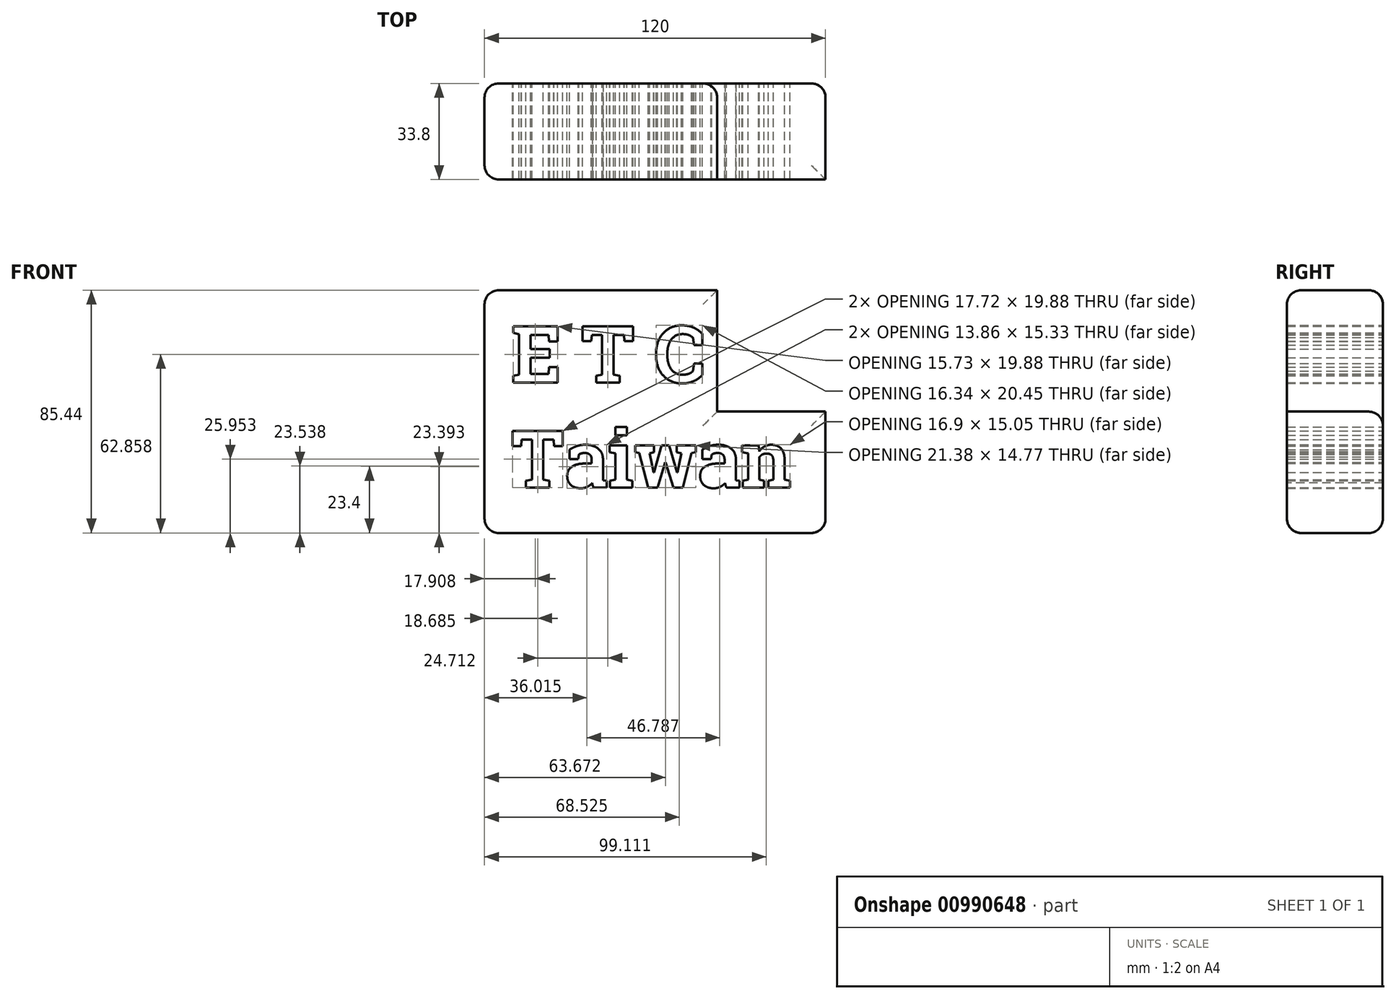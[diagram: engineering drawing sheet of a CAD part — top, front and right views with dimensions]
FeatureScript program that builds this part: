
annotation { "Feature Type Name" : "Feature", "Feature Type Description" : "" }
export const myFeature = defineFeature(function(context is Context, id is Id, definition is map)
    precondition{}
    {
        {
            var Q0;
            Q0=qCreatedBy(makeId("Front.planeOp"),FACE);
            var sketch = newSketch(context, id + "F0", { "sketchPlane" : qUnion([Q0])});
            skLineSegment(sketch, "E0.bottom", {"start": v(60, -42.72) * mm, "end": v(-60, -42.72) * mm});
            skLineSegment(sketch, "E0.top", {"start": v(60, 42.72) * mm, "end": v(-60, 42.72) * mm});
            skLineSegment(sketch, "E0.left", {"start": v(60, -42.72) * mm, "end": v(60, 42.72) * mm});
            skLineSegment(sketch, "E0.right", {"start": v(-60, -42.72) * mm, "end": v(-60, 42.72) * mm});
            skPoint(sketch, "E0.middle", {"position": v(0, 0) * mm});
            skText(sketch, "E1", { "text": "E T C \nTaiwan", "fontName": "RobotoSlab-Bold.ttf"});
            const initialGuessF0  = {"E1": [-0.05072, 0.0102, 1, 0, 0.02013]};
            skSetInitialGuess(sketch, initialGuessF0);
            skSolve(sketch);
        }
        {
            var Q0;
            Q0=makeQuery(id+"F0.imprint","IMPRINT",FACE,{"disambiguationData":[TD([[makeQuery(id+"F0.imprint","IMPRINT",EDGE,{"derivedFrom":sQuery(id+"F0.wireOp",EDGE,"E0.bottom")}),-1.0]])]});
            extrude(context, id + "F1", {"entities" : qUnion([Q0]), "depth" : 3.2 * mm, "offsetDistance" : 25 * mm});
        }
        {
            var Q0;
            Q0 = qSketchRegion(id + "F0", true);
            extrude(context, id + "F2", {"entities" : qUnion([Q0]), "operationType" : NewBodyOperationType.ADD, "oppositeDirection" : true, "depth" : 30.6 * mm, "offsetDistance" : 25 * mm});
        }
        {
            var Q0;
            Q0=makeQuery(id+"F1.opExtrude","CAP_FACE",FACE,{"disambiguationData":[OSD([sQuery(id+"F0.wireOp",EDGE,"E0.bottom"),sQuery(id+"F0.wireOp",EDGE,"E0.top"),sQuery(id+"F0.wireOp",EDGE,"E0.left"),sQuery(id+"F0.wireOp",EDGE,"E0.right"),sQuery(id+"F0.wireOp",EDGE,"E1.sketch_text.stroke-0"),sQuery(id+"F0.wireOp",EDGE,"E1.sketch_text.stroke-1"),sQuery(id+"F0.wireOp",EDGE,"E1.sketch_text.stroke-2"),sQuery(id+"F0.wireOp",EDGE,"E1.sketch_text.stroke-3"),sQuery(id+"F0.wireOp",EDGE,"E1.sketch_text.stroke-4"),sQuery(id+"F0.wireOp",EDGE,"E1.sketch_text.stroke-5"),sQuery(id+"F0.wireOp",EDGE,"E1.sketch_text.stroke-6"),sQuery(id+"F0.wireOp",EDGE,"E1.sketch_text.stroke-7"),sQuery(id+"F0.wireOp",EDGE,"E1.sketch_text.stroke-8"),sQuery(id+"F0.wireOp",EDGE,"E1.sketch_text.stroke-9"),sQuery(id+"F0.wireOp",EDGE,"E1.sketch_text.stroke-10"),sQuery(id+"F0.wireOp",EDGE,"E1.sketch_text.stroke-11"),sQuery(id+"F0.wireOp",EDGE,"E1.sketch_text.stroke-12"),sQuery(id+"F0.wireOp",EDGE,"E1.sketch_text.stroke-13"),sQuery(id+"F0.wireOp",EDGE,"E1.sketch_text.stroke-14"),sQuery(id+"F0.wireOp",EDGE,"E1.sketch_text.stroke-15"),sQuery(id+"F0.wireOp",EDGE,"E1.sketch_text.stroke-16"),sQuery(id+"F0.wireOp",EDGE,"E1.sketch_text.stroke-17"),sQuery(id+"F0.wireOp",EDGE,"E1.sketch_text.stroke-18"),sQuery(id+"F0.wireOp",EDGE,"E1.sketch_text.stroke-19"),sQuery(id+"F0.wireOp",EDGE,"E1.sketch_text.stroke-20"),sQuery(id+"F0.wireOp",EDGE,"E1.sketch_text.stroke-21"),sQuery(id+"F0.wireOp",EDGE,"E1.sketch_text.stroke-22"),sQuery(id+"F0.wireOp",EDGE,"E1.sketch_text.stroke-23"),sQuery(id+"F0.wireOp",EDGE,"E1.sketch_text.stroke-24"),sQuery(id+"F0.wireOp",EDGE,"E1.sketch_text.stroke-25"),sQuery(id+"F0.wireOp",EDGE,"E1.sketch_text.stroke-26"),sQuery(id+"F0.wireOp",EDGE,"E1.sketch_text.stroke-27"),sQuery(id+"F0.wireOp",EDGE,"E1.sketch_text.stroke-28"),sQuery(id+"F0.wireOp",EDGE,"E1.sketch_text.stroke-29"),sQuery(id+"F0.wireOp",EDGE,"E1.sketch_text.stroke-30"),sQuery(id+"F0.wireOp",EDGE,"E1.sketch_text.stroke-31"),sQuery(id+"F0.wireOp",EDGE,"E1.sketch_text.stroke-32"),sQuery(id+"F0.wireOp",EDGE,"E1.sketch_text.stroke-33"),sQuery(id+"F0.wireOp",EDGE,"E1.sketch_text.stroke-34"),sQuery(id+"F0.wireOp",EDGE,"E1.sketch_text.stroke-35"),sQuery(id+"F0.wireOp",EDGE,"E1.sketch_text.stroke-36"),sQuery(id+"F0.wireOp",EDGE,"E1.sketch_text.stroke-37"),sQuery(id+"F0.wireOp",EDGE,"E1.sketch_text.stroke-38"),sQuery(id+"F0.wireOp",EDGE,"E1.sketch_text.stroke-39"),sQuery(id+"F0.wireOp",EDGE,"E1.sketch_text.stroke-40"),sQuery(id+"F0.wireOp",EDGE,"E1.sketch_text.stroke-41"),sQuery(id+"F0.wireOp",EDGE,"E1.sketch_text.stroke-42"),sQuery(id+"F0.wireOp",EDGE,"E1.sketch_text.stroke-43"),sQuery(id+"F0.wireOp",EDGE,"E1.sketch_text.stroke-44"),sQuery(id+"F0.wireOp",EDGE,"E1.sketch_text.stroke-45"),sQuery(id+"F0.wireOp",EDGE,"E1.sketch_text.stroke-46"),sQuery(id+"F0.wireOp",EDGE,"E1.sketch_text.stroke-47"),sQuery(id+"F0.wireOp",EDGE,"E1.sketch_text.stroke-48"),sQuery(id+"F0.wireOp",EDGE,"E1.sketch_text.stroke-49"),sQuery(id+"F0.wireOp",EDGE,"E1.sketch_text.stroke-50"),sQuery(id+"F0.wireOp",EDGE,"E1.sketch_text.stroke-51"),sQuery(id+"F0.wireOp",EDGE,"E1.sketch_text.stroke-52"),sQuery(id+"F0.wireOp",EDGE,"E1.sketch_text.stroke-53"),sQuery(id+"F0.wireOp",EDGE,"E1.sketch_text.stroke-54"),sQuery(id+"F0.wireOp",EDGE,"E1.sketch_text.stroke-55"),sQuery(id+"F0.wireOp",EDGE,"E1.sketch_text.stroke-56"),sQuery(id+"F0.wireOp",EDGE,"E1.sketch_text.stroke-57"),sQuery(id+"F0.wireOp",EDGE,"E1.sketch_text.stroke-58"),sQuery(id+"F0.wireOp",EDGE,"E1.sketch_text.stroke-59"),sQuery(id+"F0.wireOp",EDGE,"E1.sketch_text.stroke-60"),sQuery(id+"F0.wireOp",EDGE,"E1.sketch_text.stroke-61"),sQuery(id+"F0.wireOp",EDGE,"E1.sketch_text.stroke-62"),sQuery(id+"F0.wireOp",EDGE,"E1.sketch_text.stroke-63"),sQuery(id+"F0.wireOp",EDGE,"E1.sketch_text.stroke-64"),sQuery(id+"F0.wireOp",EDGE,"E1.sketch_text.stroke-65"),sQuery(id+"F0.wireOp",EDGE,"E1.sketch_text.stroke-66"),sQuery(id+"F0.wireOp",EDGE,"E1.sketch_text.stroke-67"),sQuery(id+"F0.wireOp",EDGE,"E1.sketch_text.stroke-68"),sQuery(id+"F0.wireOp",EDGE,"E1.sketch_text.stroke-69"),sQuery(id+"F0.wireOp",EDGE,"E1.sketch_text.stroke-70"),sQuery(id+"F0.wireOp",EDGE,"E1.sketch_text.stroke-71"),sQuery(id+"F0.wireOp",EDGE,"E1.sketch_text.stroke-72"),sQuery(id+"F0.wireOp",EDGE,"E1.sketch_text.stroke-73"),sQuery(id+"F0.wireOp",EDGE,"E1.sketch_text.stroke-74"),sQuery(id+"F0.wireOp",EDGE,"E1.sketch_text.stroke-75"),sQuery(id+"F0.wireOp",EDGE,"E1.sketch_text.stroke-76"),sQuery(id+"F0.wireOp",EDGE,"E1.sketch_text.stroke-77"),sQuery(id+"F0.wireOp",EDGE,"E1.sketch_text.stroke-78"),sQuery(id+"F0.wireOp",EDGE,"E1.sketch_text.stroke-79"),sQuery(id+"F0.wireOp",EDGE,"E1.sketch_text.stroke-80"),sQuery(id+"F0.wireOp",EDGE,"E1.sketch_text.stroke-81"),sQuery(id+"F0.wireOp",EDGE,"E1.sketch_text.stroke-82"),sQuery(id+"F0.wireOp",EDGE,"E1.sketch_text.stroke-83"),sQuery(id+"F0.wireOp",EDGE,"E1.sketch_text.stroke-84"),sQuery(id+"F0.wireOp",EDGE,"E1.sketch_text.stroke-85"),sQuery(id+"F0.wireOp",EDGE,"E1.sketch_text.stroke-86"),sQuery(id+"F0.wireOp",EDGE,"E1.sketch_text.stroke-87"),sQuery(id+"F0.wireOp",EDGE,"E1.sketch_text.stroke-88"),sQuery(id+"F0.wireOp",EDGE,"E1.sketch_text.stroke-89"),sQuery(id+"F0.wireOp",EDGE,"E1.sketch_text.stroke-90"),sQuery(id+"F0.wireOp",EDGE,"E1.sketch_text.stroke-91"),sQuery(id+"F0.wireOp",EDGE,"E1.sketch_text.stroke-92"),sQuery(id+"F0.wireOp",EDGE,"E1.sketch_text.stroke-93"),sQuery(id+"F0.wireOp",EDGE,"E1.sketch_text.stroke-94"),sQuery(id+"F0.wireOp",EDGE,"E1.sketch_text.stroke-95"),sQuery(id+"F0.wireOp",EDGE,"E1.sketch_text.stroke-96"),sQuery(id+"F0.wireOp",EDGE,"E1.sketch_text.stroke-97"),sQuery(id+"F0.wireOp",EDGE,"E1.sketch_text.stroke-98"),sQuery(id+"F0.wireOp",EDGE,"E1.sketch_text.stroke-99"),sQuery(id+"F0.wireOp",EDGE,"E1.sketch_text.stroke-100"),sQuery(id+"F0.wireOp",EDGE,"E1.sketch_text.stroke-101"),sQuery(id+"F0.wireOp",EDGE,"E1.sketch_text.stroke-102"),sQuery(id+"F0.wireOp",EDGE,"E1.sketch_text.stroke-103"),sQuery(id+"F0.wireOp",EDGE,"E1.sketch_text.stroke-112"),sQuery(id+"F0.wireOp",EDGE,"E1.sketch_text.stroke-113"),sQuery(id+"F0.wireOp",EDGE,"E1.sketch_text.stroke-114"),sQuery(id+"F0.wireOp",EDGE,"E1.sketch_text.stroke-115"),sQuery(id+"F0.wireOp",EDGE,"E1.sketch_text.stroke-116"),sQuery(id+"F0.wireOp",EDGE,"E1.sketch_text.stroke-117"),sQuery(id+"F0.wireOp",EDGE,"E1.sketch_text.stroke-118"),sQuery(id+"F0.wireOp",EDGE,"E1.sketch_text.stroke-119"),sQuery(id+"F0.wireOp",EDGE,"E1.sketch_text.stroke-120"),sQuery(id+"F0.wireOp",EDGE,"E1.sketch_text.stroke-121"),sQuery(id+"F0.wireOp",EDGE,"E1.sketch_text.stroke-122"),sQuery(id+"F0.wireOp",EDGE,"E1.sketch_text.stroke-123"),sQuery(id+"F0.wireOp",EDGE,"E1.sketch_text.stroke-124"),sQuery(id+"F0.wireOp",EDGE,"E1.sketch_text.stroke-125"),sQuery(id+"F0.wireOp",EDGE,"E1.sketch_text.stroke-126"),sQuery(id+"F0.wireOp",EDGE,"E1.sketch_text.stroke-127"),sQuery(id+"F0.wireOp",EDGE,"E1.sketch_text.stroke-128"),sQuery(id+"F0.wireOp",EDGE,"E1.sketch_text.stroke-129"),sQuery(id+"F0.wireOp",EDGE,"E1.sketch_text.stroke-130"),sQuery(id+"F0.wireOp",EDGE,"E1.sketch_text.stroke-131"),sQuery(id+"F0.wireOp",EDGE,"E1.sketch_text.stroke-132"),sQuery(id+"F0.wireOp",EDGE,"E1.sketch_text.stroke-133"),sQuery(id+"F0.wireOp",EDGE,"E1.sketch_text.stroke-134"),sQuery(id+"F0.wireOp",EDGE,"E1.sketch_text.stroke-135"),sQuery(id+"F0.wireOp",EDGE,"E1.sketch_text.stroke-136"),sQuery(id+"F0.wireOp",EDGE,"E1.sketch_text.stroke-137"),sQuery(id+"F0.wireOp",EDGE,"E1.sketch_text.stroke-138"),sQuery(id+"F0.wireOp",EDGE,"E1.sketch_text.stroke-139"),sQuery(id+"F0.wireOp",EDGE,"E1.sketch_text.stroke-140"),sQuery(id+"F0.wireOp",EDGE,"E1.sketch_text.stroke-141"),sQuery(id+"F0.wireOp",EDGE,"E1.sketch_text.stroke-142"),sQuery(id+"F0.wireOp",EDGE,"E1.sketch_text.stroke-143"),sQuery(id+"F0.wireOp",EDGE,"E1.sketch_text.stroke-144"),sQuery(id+"F0.wireOp",EDGE,"E1.sketch_text.stroke-145"),sQuery(id+"F0.wireOp",EDGE,"E1.sketch_text.stroke-146"),sQuery(id+"F0.wireOp",EDGE,"E1.sketch_text.stroke-147"),sQuery(id+"F0.wireOp",EDGE,"E1.sketch_text.stroke-148"),sQuery(id+"F0.wireOp",EDGE,"E1.sketch_text.stroke-149"),sQuery(id+"F0.wireOp",EDGE,"E1.sketch_text.stroke-150"),sQuery(id+"F0.wireOp",EDGE,"E1.sketch_text.stroke-151"),sQuery(id+"F0.wireOp",EDGE,"E1.sketch_text.stroke-152"),sQuery(id+"F0.wireOp",EDGE,"E1.sketch_text.stroke-153"),sQuery(id+"F0.wireOp",EDGE,"E1.sketch_text.stroke-154"),sQuery(id+"F0.wireOp",EDGE,"E1.sketch_text.stroke-155"),sQuery(id+"F0.wireOp",EDGE,"E1.sketch_text.stroke-156"),sQuery(id+"F0.wireOp",EDGE,"E1.sketch_text.stroke-157"),sQuery(id+"F0.wireOp",EDGE,"E1.sketch_text.stroke-158"),sQuery(id+"F0.wireOp",EDGE,"E1.sketch_text.stroke-159"),sQuery(id+"F0.wireOp",EDGE,"E1.sketch_text.stroke-160"),sQuery(id+"F0.wireOp",EDGE,"E1.sketch_text.stroke-161"),sQuery(id+"F0.wireOp",EDGE,"E1.sketch_text.stroke-162"),sQuery(id+"F0.wireOp",EDGE,"E1.sketch_text.stroke-163"),sQuery(id+"F0.wireOp",EDGE,"E1.sketch_text.stroke-164"),sQuery(id+"F0.wireOp",EDGE,"E1.sketch_text.stroke-165"),sQuery(id+"F0.wireOp",EDGE,"E1.sketch_text.stroke-166"),sQuery(id+"F0.wireOp",EDGE,"E1.sketch_text.stroke-167"),sQuery(id+"F0.wireOp",EDGE,"E1.sketch_text.stroke-168"),sQuery(id+"F0.wireOp",EDGE,"E1.sketch_text.stroke-169"),sQuery(id+"F0.wireOp",EDGE,"E1.sketch_text.stroke-170"),sQuery(id+"F0.wireOp",EDGE,"E1.sketch_text.stroke-171"),sQuery(id+"F0.wireOp",EDGE,"E1.sketch_text.stroke-172"),sQuery(id+"F0.wireOp",EDGE,"E1.sketch_text.stroke-173"),sQuery(id+"F0.wireOp",EDGE,"E1.sketch_text.stroke-174"),sQuery(id+"F0.wireOp",EDGE,"E1.sketch_text.stroke-175"),sQuery(id+"F0.wireOp",EDGE,"E1.sketch_text.stroke-176"),sQuery(id+"F0.wireOp",EDGE,"E1.sketch_text.stroke-185"),sQuery(id+"F0.wireOp",EDGE,"E1.sketch_text.stroke-186"),sQuery(id+"F0.wireOp",EDGE,"E1.sketch_text.stroke-187"),sQuery(id+"F0.wireOp",EDGE,"E1.sketch_text.stroke-188"),sQuery(id+"F0.wireOp",EDGE,"E1.sketch_text.stroke-189"),sQuery(id+"F0.wireOp",EDGE,"E1.sketch_text.stroke-190"),sQuery(id+"F0.wireOp",EDGE,"E1.sketch_text.stroke-191"),sQuery(id+"F0.wireOp",EDGE,"E1.sketch_text.stroke-192"),sQuery(id+"F0.wireOp",EDGE,"E1.sketch_text.stroke-193"),sQuery(id+"F0.wireOp",EDGE,"E1.sketch_text.stroke-194"),sQuery(id+"F0.wireOp",EDGE,"E1.sketch_text.stroke-195"),sQuery(id+"F0.wireOp",EDGE,"E1.sketch_text.stroke-196"),sQuery(id+"F0.wireOp",EDGE,"E1.sketch_text.stroke-197"),sQuery(id+"F0.wireOp",EDGE,"E1.sketch_text.stroke-198"),sQuery(id+"F0.wireOp",EDGE,"E1.sketch_text.stroke-199"),sQuery(id+"F0.wireOp",EDGE,"E1.sketch_text.stroke-200"),sQuery(id+"F0.wireOp",EDGE,"E1.sketch_text.stroke-201"),sQuery(id+"F0.wireOp",EDGE,"E1.sketch_text.stroke-202"),sQuery(id+"F0.wireOp",EDGE,"E1.sketch_text.stroke-203"),sQuery(id+"F0.wireOp",EDGE,"E1.sketch_text.stroke-204"),sQuery(id+"F0.wireOp",EDGE,"E1.sketch_text.stroke-205"),sQuery(id+"F0.wireOp",EDGE,"E1.sketch_text.stroke-206"),sQuery(id+"F0.wireOp",EDGE,"E1.sketch_text.stroke-207"),sQuery(id+"F0.wireOp",EDGE,"E1.sketch_text.stroke-208"),sQuery(id+"F0.wireOp",EDGE,"E1.sketch_text.stroke-209"),sQuery(id+"F0.wireOp",EDGE,"E1.sketch_text.stroke-210")])],"isStart":false});
            var sketch = newSketch(context, id + "F3", { "sketchPlane" : qUnion([Q0])});
            skLineSegment(sketch, "E2.bottom", {"start": v(60, 42.72) * mm, "end": v(21.87, 42.72) * mm});
            skLineSegment(sketch, "E2.top", {"start": v(60, 0) * mm, "end": v(21.87, 0) * mm});
            skLineSegment(sketch, "E2.left", {"start": v(60, 42.72) * mm, "end": v(60, 0) * mm});
            skLineSegment(sketch, "E2.right", {"start": v(21.87, 42.72) * mm, "end": v(21.87, 0) * mm});
            skSolve(sketch);
        }
        {
            var Q0;
            Q0=makeQuery(id+"F3.imprint","IMPRINT",FACE,{"disambiguationData":[TD([[makeQuery(id+"F3.imprint","IMPRINT",EDGE,{"derivedFrom":sQuery(id+"F3.wireOp",EDGE,"E2.bottom")}),1.0]])]});
            extrude(context, id + "F4", {"entities" : qUnion([Q0]), "operationType" : NewBodyOperationType.REMOVE, "oppositeDirection" : true, "depth" : 35.3 * mm, "offsetDistance" : 25 * mm});
        }
        {
            var Q0;
            Q0=makeQuery(id+"F4.boolean.opBoolean","COPY",EDGE,{"derivedFrom":makeQuery(id+"F4.opExtrude","SWEPT_EDGE",EDGE,{"disambiguationData":[OSD([sQuery(id+"F0.wireOp",EDGE,"E0.top"),sQuery(id+"F3.wireOp",EDGE,"E2.bottom"),sQuery(id+"F3.wireOp",EDGE,"E2.right")])]})});
            var Q1;
            Q1=makeQuery(id+"F4.boolean.opBoolean","COPY",EDGE,{"derivedFrom":makeQuery(id+"F4.opExtrude","SWEPT_EDGE",EDGE,{"disambiguationData":[OSD([sQuery(id+"F0.wireOp",EDGE,"E0.left"),sQuery(id+"F3.wireOp",EDGE,"E2.top"),sQuery(id+"F3.wireOp",EDGE,"E2.left")])]})});
            var Q2;
            {var subQ0=sQuery(id+"F0.wireOp",EDGE,"E0.left");var subQ1=sQuery(id+"F0.wireOp",EDGE,"E0.bottom");Q2=makeQuery(id+"F2.boolean.opBoolean","MERGE",EDGE,{"derivedFrom":[makeQuery(id+"F1.opExtrude","SWEPT_EDGE",EDGE,{"disambiguationData":[OSD([subQ1,subQ0])]}),makeQuery(id+"F2.opExtrude","SWEPT_EDGE",EDGE,{"disambiguationData":[OSD([subQ1,subQ0])]})]});}
            var Q3;
            {var subQ0=sQuery(id+"F0.wireOp",EDGE,"E0.bottom");Q3=makeQuery(id+"F2.boolean.opBoolean","MERGE",FACE,{"derivedFrom":[makeQuery(id+"F1.opExtrude","SWEPT_FACE",FACE,{"disambiguationData":[OSD([subQ0])]}),makeQuery(id+"F2.opExtrude","SWEPT_FACE",FACE,{"disambiguationData":[OSD([subQ0])]})]});}
            var Q4;
            {var subQ0=sQuery(id+"F0.wireOp",EDGE,"E0.right");var subQ1=sQuery(id+"F0.wireOp",EDGE,"E0.bottom");Q4=makeQuery(id+"F2.boolean.opBoolean","MERGE",EDGE,{"derivedFrom":[makeQuery(id+"F1.opExtrude","SWEPT_EDGE",EDGE,{"disambiguationData":[OSD([subQ1,subQ0])]}),makeQuery(id+"F2.opExtrude","SWEPT_EDGE",EDGE,{"disambiguationData":[OSD([subQ1,subQ0])]})]});}
            var Q5;
            Q5=makeQuery(id+"F1.opExtrude","CAP_EDGE",EDGE,{"disambiguationData":[OSD([sQuery(id+"F0.wireOp",EDGE,"E0.right")])],"isStart":false});
            var Q6;
            Q6=makeQuery(id+"F2.opExtrude","CAP_EDGE",EDGE,{"disambiguationData":[OSD([sQuery(id+"F0.wireOp",EDGE,"E0.right")])],"isStart":false});
            var Q7;
            {var subQ0=sQuery(id+"F0.wireOp",EDGE,"E0.right");var subQ1=sQuery(id+"F0.wireOp",EDGE,"E0.top");Q7=makeQuery(id+"F2.boolean.opBoolean","MERGE",EDGE,{"derivedFrom":[makeQuery(id+"F1.opExtrude","SWEPT_EDGE",EDGE,{"disambiguationData":[OSD([subQ1,subQ0])]}),makeQuery(id+"F2.opExtrude","SWEPT_EDGE",EDGE,{"disambiguationData":[OSD([subQ1,subQ0])]})]});}
            var Q8;
            Q8=makeQuery(id+"F1.opExtrude","CAP_EDGE",EDGE,{"disambiguationData":[OSD([sQuery(id+"F0.wireOp",EDGE,"E0.top")])],"isStart":false});
            var Q9;
            Q9=makeQuery(id+"F2.opExtrude","CAP_EDGE",EDGE,{"disambiguationData":[OSD([sQuery(id+"F0.wireOp",EDGE,"E0.top")])],"isStart":false});
            var Q10;
            Q10=makeQuery(id+"F4.boolean.opBoolean","COPY",EDGE,{"derivedFrom":makeQuery(id+"F4.opExtrude","CAP_EDGE",EDGE,{"disambiguationData":[OSD([sQuery(id+"F3.wireOp",EDGE,"E2.top")])],"isStart":true})});
            var Q11;
            Q11=makeQuery(id+"F4.boolean.opBoolean","COPY",EDGE,{"derivedFrom":makeQuery(id+"F4.opExtrude","CAP_EDGE",EDGE,{"disambiguationData":[OSD([sQuery(id+"F3.wireOp",EDGE,"E2.right")])],"isStart":true})});
            var Q12;
            Q12=makeQuery(id+"F2.opExtrude","CAP_EDGE",EDGE,{"disambiguationData":[OSD([sQuery(id+"F0.wireOp",EDGE,"E0.left")])],"isStart":false});
            var Q13;
            Q13=makeQuery(id+"F4.boolean.opBoolean","INTERSECT",EDGE,{"derivedFrom":[makeQuery(id+"F2.opExtrude","CAP_FACE",FACE,{"disambiguationData":[OSD([sQuery(id+"F0.wireOp",EDGE,"E0.bottom"),sQuery(id+"F0.wireOp",EDGE,"E0.top"),sQuery(id+"F0.wireOp",EDGE,"E0.left"),sQuery(id+"F0.wireOp",EDGE,"E0.right"),sQuery(id+"F0.wireOp",EDGE,"E1.sketch_text.stroke-0"),sQuery(id+"F0.wireOp",EDGE,"E1.sketch_text.stroke-1"),sQuery(id+"F0.wireOp",EDGE,"E1.sketch_text.stroke-2"),sQuery(id+"F0.wireOp",EDGE,"E1.sketch_text.stroke-3"),sQuery(id+"F0.wireOp",EDGE,"E1.sketch_text.stroke-4"),sQuery(id+"F0.wireOp",EDGE,"E1.sketch_text.stroke-5"),sQuery(id+"F0.wireOp",EDGE,"E1.sketch_text.stroke-6"),sQuery(id+"F0.wireOp",EDGE,"E1.sketch_text.stroke-7"),sQuery(id+"F0.wireOp",EDGE,"E1.sketch_text.stroke-8"),sQuery(id+"F0.wireOp",EDGE,"E1.sketch_text.stroke-9"),sQuery(id+"F0.wireOp",EDGE,"E1.sketch_text.stroke-10"),sQuery(id+"F0.wireOp",EDGE,"E1.sketch_text.stroke-11"),sQuery(id+"F0.wireOp",EDGE,"E1.sketch_text.stroke-12"),sQuery(id+"F0.wireOp",EDGE,"E1.sketch_text.stroke-13"),sQuery(id+"F0.wireOp",EDGE,"E1.sketch_text.stroke-14"),sQuery(id+"F0.wireOp",EDGE,"E1.sketch_text.stroke-15"),sQuery(id+"F0.wireOp",EDGE,"E1.sketch_text.stroke-16"),sQuery(id+"F0.wireOp",EDGE,"E1.sketch_text.stroke-17"),sQuery(id+"F0.wireOp",EDGE,"E1.sketch_text.stroke-18"),sQuery(id+"F0.wireOp",EDGE,"E1.sketch_text.stroke-19"),sQuery(id+"F0.wireOp",EDGE,"E1.sketch_text.stroke-20"),sQuery(id+"F0.wireOp",EDGE,"E1.sketch_text.stroke-21"),sQuery(id+"F0.wireOp",EDGE,"E1.sketch_text.stroke-22"),sQuery(id+"F0.wireOp",EDGE,"E1.sketch_text.stroke-23"),sQuery(id+"F0.wireOp",EDGE,"E1.sketch_text.stroke-24"),sQuery(id+"F0.wireOp",EDGE,"E1.sketch_text.stroke-25"),sQuery(id+"F0.wireOp",EDGE,"E1.sketch_text.stroke-26"),sQuery(id+"F0.wireOp",EDGE,"E1.sketch_text.stroke-27"),sQuery(id+"F0.wireOp",EDGE,"E1.sketch_text.stroke-28"),sQuery(id+"F0.wireOp",EDGE,"E1.sketch_text.stroke-29"),sQuery(id+"F0.wireOp",EDGE,"E1.sketch_text.stroke-30"),sQuery(id+"F0.wireOp",EDGE,"E1.sketch_text.stroke-31"),sQuery(id+"F0.wireOp",EDGE,"E1.sketch_text.stroke-32"),sQuery(id+"F0.wireOp",EDGE,"E1.sketch_text.stroke-33"),sQuery(id+"F0.wireOp",EDGE,"E1.sketch_text.stroke-34"),sQuery(id+"F0.wireOp",EDGE,"E1.sketch_text.stroke-35"),sQuery(id+"F0.wireOp",EDGE,"E1.sketch_text.stroke-36"),sQuery(id+"F0.wireOp",EDGE,"E1.sketch_text.stroke-37"),sQuery(id+"F0.wireOp",EDGE,"E1.sketch_text.stroke-38"),sQuery(id+"F0.wireOp",EDGE,"E1.sketch_text.stroke-39"),sQuery(id+"F0.wireOp",EDGE,"E1.sketch_text.stroke-40"),sQuery(id+"F0.wireOp",EDGE,"E1.sketch_text.stroke-41"),sQuery(id+"F0.wireOp",EDGE,"E1.sketch_text.stroke-42"),sQuery(id+"F0.wireOp",EDGE,"E1.sketch_text.stroke-43"),sQuery(id+"F0.wireOp",EDGE,"E1.sketch_text.stroke-44"),sQuery(id+"F0.wireOp",EDGE,"E1.sketch_text.stroke-45"),sQuery(id+"F0.wireOp",EDGE,"E1.sketch_text.stroke-46"),sQuery(id+"F0.wireOp",EDGE,"E1.sketch_text.stroke-47"),sQuery(id+"F0.wireOp",EDGE,"E1.sketch_text.stroke-48"),sQuery(id+"F0.wireOp",EDGE,"E1.sketch_text.stroke-49"),sQuery(id+"F0.wireOp",EDGE,"E1.sketch_text.stroke-50"),sQuery(id+"F0.wireOp",EDGE,"E1.sketch_text.stroke-51"),sQuery(id+"F0.wireOp",EDGE,"E1.sketch_text.stroke-52"),sQuery(id+"F0.wireOp",EDGE,"E1.sketch_text.stroke-53"),sQuery(id+"F0.wireOp",EDGE,"E1.sketch_text.stroke-54"),sQuery(id+"F0.wireOp",EDGE,"E1.sketch_text.stroke-55"),sQuery(id+"F0.wireOp",EDGE,"E1.sketch_text.stroke-56"),sQuery(id+"F0.wireOp",EDGE,"E1.sketch_text.stroke-57"),sQuery(id+"F0.wireOp",EDGE,"E1.sketch_text.stroke-58"),sQuery(id+"F0.wireOp",EDGE,"E1.sketch_text.stroke-59"),sQuery(id+"F0.wireOp",EDGE,"E1.sketch_text.stroke-60"),sQuery(id+"F0.wireOp",EDGE,"E1.sketch_text.stroke-61"),sQuery(id+"F0.wireOp",EDGE,"E1.sketch_text.stroke-62"),sQuery(id+"F0.wireOp",EDGE,"E1.sketch_text.stroke-63"),sQuery(id+"F0.wireOp",EDGE,"E1.sketch_text.stroke-64"),sQuery(id+"F0.wireOp",EDGE,"E1.sketch_text.stroke-65"),sQuery(id+"F0.wireOp",EDGE,"E1.sketch_text.stroke-66"),sQuery(id+"F0.wireOp",EDGE,"E1.sketch_text.stroke-67"),sQuery(id+"F0.wireOp",EDGE,"E1.sketch_text.stroke-68"),sQuery(id+"F0.wireOp",EDGE,"E1.sketch_text.stroke-69"),sQuery(id+"F0.wireOp",EDGE,"E1.sketch_text.stroke-70"),sQuery(id+"F0.wireOp",EDGE,"E1.sketch_text.stroke-71"),sQuery(id+"F0.wireOp",EDGE,"E1.sketch_text.stroke-72"),sQuery(id+"F0.wireOp",EDGE,"E1.sketch_text.stroke-73"),sQuery(id+"F0.wireOp",EDGE,"E1.sketch_text.stroke-74"),sQuery(id+"F0.wireOp",EDGE,"E1.sketch_text.stroke-75"),sQuery(id+"F0.wireOp",EDGE,"E1.sketch_text.stroke-76"),sQuery(id+"F0.wireOp",EDGE,"E1.sketch_text.stroke-77"),sQuery(id+"F0.wireOp",EDGE,"E1.sketch_text.stroke-78"),sQuery(id+"F0.wireOp",EDGE,"E1.sketch_text.stroke-79"),sQuery(id+"F0.wireOp",EDGE,"E1.sketch_text.stroke-80"),sQuery(id+"F0.wireOp",EDGE,"E1.sketch_text.stroke-81"),sQuery(id+"F0.wireOp",EDGE,"E1.sketch_text.stroke-82"),sQuery(id+"F0.wireOp",EDGE,"E1.sketch_text.stroke-83"),sQuery(id+"F0.wireOp",EDGE,"E1.sketch_text.stroke-84"),sQuery(id+"F0.wireOp",EDGE,"E1.sketch_text.stroke-85"),sQuery(id+"F0.wireOp",EDGE,"E1.sketch_text.stroke-86"),sQuery(id+"F0.wireOp",EDGE,"E1.sketch_text.stroke-87"),sQuery(id+"F0.wireOp",EDGE,"E1.sketch_text.stroke-88"),sQuery(id+"F0.wireOp",EDGE,"E1.sketch_text.stroke-89"),sQuery(id+"F0.wireOp",EDGE,"E1.sketch_text.stroke-90"),sQuery(id+"F0.wireOp",EDGE,"E1.sketch_text.stroke-91"),sQuery(id+"F0.wireOp",EDGE,"E1.sketch_text.stroke-92"),sQuery(id+"F0.wireOp",EDGE,"E1.sketch_text.stroke-93"),sQuery(id+"F0.wireOp",EDGE,"E1.sketch_text.stroke-94"),sQuery(id+"F0.wireOp",EDGE,"E1.sketch_text.stroke-95"),sQuery(id+"F0.wireOp",EDGE,"E1.sketch_text.stroke-96"),sQuery(id+"F0.wireOp",EDGE,"E1.sketch_text.stroke-97"),sQuery(id+"F0.wireOp",EDGE,"E1.sketch_text.stroke-98"),sQuery(id+"F0.wireOp",EDGE,"E1.sketch_text.stroke-99"),sQuery(id+"F0.wireOp",EDGE,"E1.sketch_text.stroke-100"),sQuery(id+"F0.wireOp",EDGE,"E1.sketch_text.stroke-101"),sQuery(id+"F0.wireOp",EDGE,"E1.sketch_text.stroke-102"),sQuery(id+"F0.wireOp",EDGE,"E1.sketch_text.stroke-103"),sQuery(id+"F0.wireOp",EDGE,"E1.sketch_text.stroke-112"),sQuery(id+"F0.wireOp",EDGE,"E1.sketch_text.stroke-113"),sQuery(id+"F0.wireOp",EDGE,"E1.sketch_text.stroke-114"),sQuery(id+"F0.wireOp",EDGE,"E1.sketch_text.stroke-115"),sQuery(id+"F0.wireOp",EDGE,"E1.sketch_text.stroke-116"),sQuery(id+"F0.wireOp",EDGE,"E1.sketch_text.stroke-117"),sQuery(id+"F0.wireOp",EDGE,"E1.sketch_text.stroke-118"),sQuery(id+"F0.wireOp",EDGE,"E1.sketch_text.stroke-119"),sQuery(id+"F0.wireOp",EDGE,"E1.sketch_text.stroke-120"),sQuery(id+"F0.wireOp",EDGE,"E1.sketch_text.stroke-121"),sQuery(id+"F0.wireOp",EDGE,"E1.sketch_text.stroke-122"),sQuery(id+"F0.wireOp",EDGE,"E1.sketch_text.stroke-123"),sQuery(id+"F0.wireOp",EDGE,"E1.sketch_text.stroke-124"),sQuery(id+"F0.wireOp",EDGE,"E1.sketch_text.stroke-125"),sQuery(id+"F0.wireOp",EDGE,"E1.sketch_text.stroke-126"),sQuery(id+"F0.wireOp",EDGE,"E1.sketch_text.stroke-127"),sQuery(id+"F0.wireOp",EDGE,"E1.sketch_text.stroke-128"),sQuery(id+"F0.wireOp",EDGE,"E1.sketch_text.stroke-129"),sQuery(id+"F0.wireOp",EDGE,"E1.sketch_text.stroke-130"),sQuery(id+"F0.wireOp",EDGE,"E1.sketch_text.stroke-131"),sQuery(id+"F0.wireOp",EDGE,"E1.sketch_text.stroke-132"),sQuery(id+"F0.wireOp",EDGE,"E1.sketch_text.stroke-133"),sQuery(id+"F0.wireOp",EDGE,"E1.sketch_text.stroke-134"),sQuery(id+"F0.wireOp",EDGE,"E1.sketch_text.stroke-135"),sQuery(id+"F0.wireOp",EDGE,"E1.sketch_text.stroke-136"),sQuery(id+"F0.wireOp",EDGE,"E1.sketch_text.stroke-137"),sQuery(id+"F0.wireOp",EDGE,"E1.sketch_text.stroke-138"),sQuery(id+"F0.wireOp",EDGE,"E1.sketch_text.stroke-139"),sQuery(id+"F0.wireOp",EDGE,"E1.sketch_text.stroke-140"),sQuery(id+"F0.wireOp",EDGE,"E1.sketch_text.stroke-141"),sQuery(id+"F0.wireOp",EDGE,"E1.sketch_text.stroke-142"),sQuery(id+"F0.wireOp",EDGE,"E1.sketch_text.stroke-143"),sQuery(id+"F0.wireOp",EDGE,"E1.sketch_text.stroke-144"),sQuery(id+"F0.wireOp",EDGE,"E1.sketch_text.stroke-145"),sQuery(id+"F0.wireOp",EDGE,"E1.sketch_text.stroke-146"),sQuery(id+"F0.wireOp",EDGE,"E1.sketch_text.stroke-147"),sQuery(id+"F0.wireOp",EDGE,"E1.sketch_text.stroke-148"),sQuery(id+"F0.wireOp",EDGE,"E1.sketch_text.stroke-149"),sQuery(id+"F0.wireOp",EDGE,"E1.sketch_text.stroke-150"),sQuery(id+"F0.wireOp",EDGE,"E1.sketch_text.stroke-151"),sQuery(id+"F0.wireOp",EDGE,"E1.sketch_text.stroke-152"),sQuery(id+"F0.wireOp",EDGE,"E1.sketch_text.stroke-153"),sQuery(id+"F0.wireOp",EDGE,"E1.sketch_text.stroke-154"),sQuery(id+"F0.wireOp",EDGE,"E1.sketch_text.stroke-155"),sQuery(id+"F0.wireOp",EDGE,"E1.sketch_text.stroke-156"),sQuery(id+"F0.wireOp",EDGE,"E1.sketch_text.stroke-157"),sQuery(id+"F0.wireOp",EDGE,"E1.sketch_text.stroke-158"),sQuery(id+"F0.wireOp",EDGE,"E1.sketch_text.stroke-159"),sQuery(id+"F0.wireOp",EDGE,"E1.sketch_text.stroke-160"),sQuery(id+"F0.wireOp",EDGE,"E1.sketch_text.stroke-161"),sQuery(id+"F0.wireOp",EDGE,"E1.sketch_text.stroke-162"),sQuery(id+"F0.wireOp",EDGE,"E1.sketch_text.stroke-163"),sQuery(id+"F0.wireOp",EDGE,"E1.sketch_text.stroke-164"),sQuery(id+"F0.wireOp",EDGE,"E1.sketch_text.stroke-165"),sQuery(id+"F0.wireOp",EDGE,"E1.sketch_text.stroke-166"),sQuery(id+"F0.wireOp",EDGE,"E1.sketch_text.stroke-167"),sQuery(id+"F0.wireOp",EDGE,"E1.sketch_text.stroke-168"),sQuery(id+"F0.wireOp",EDGE,"E1.sketch_text.stroke-169"),sQuery(id+"F0.wireOp",EDGE,"E1.sketch_text.stroke-170"),sQuery(id+"F0.wireOp",EDGE,"E1.sketch_text.stroke-171"),sQuery(id+"F0.wireOp",EDGE,"E1.sketch_text.stroke-172"),sQuery(id+"F0.wireOp",EDGE,"E1.sketch_text.stroke-173"),sQuery(id+"F0.wireOp",EDGE,"E1.sketch_text.stroke-174"),sQuery(id+"F0.wireOp",EDGE,"E1.sketch_text.stroke-175"),sQuery(id+"F0.wireOp",EDGE,"E1.sketch_text.stroke-176"),sQuery(id+"F0.wireOp",EDGE,"E1.sketch_text.stroke-185"),sQuery(id+"F0.wireOp",EDGE,"E1.sketch_text.stroke-186"),sQuery(id+"F0.wireOp",EDGE,"E1.sketch_text.stroke-187"),sQuery(id+"F0.wireOp",EDGE,"E1.sketch_text.stroke-188"),sQuery(id+"F0.wireOp",EDGE,"E1.sketch_text.stroke-189"),sQuery(id+"F0.wireOp",EDGE,"E1.sketch_text.stroke-190"),sQuery(id+"F0.wireOp",EDGE,"E1.sketch_text.stroke-191"),sQuery(id+"F0.wireOp",EDGE,"E1.sketch_text.stroke-192"),sQuery(id+"F0.wireOp",EDGE,"E1.sketch_text.stroke-193"),sQuery(id+"F0.wireOp",EDGE,"E1.sketch_text.stroke-194"),sQuery(id+"F0.wireOp",EDGE,"E1.sketch_text.stroke-195"),sQuery(id+"F0.wireOp",EDGE,"E1.sketch_text.stroke-196"),sQuery(id+"F0.wireOp",EDGE,"E1.sketch_text.stroke-197"),sQuery(id+"F0.wireOp",EDGE,"E1.sketch_text.stroke-198"),sQuery(id+"F0.wireOp",EDGE,"E1.sketch_text.stroke-199"),sQuery(id+"F0.wireOp",EDGE,"E1.sketch_text.stroke-200"),sQuery(id+"F0.wireOp",EDGE,"E1.sketch_text.stroke-201"),sQuery(id+"F0.wireOp",EDGE,"E1.sketch_text.stroke-202"),sQuery(id+"F0.wireOp",EDGE,"E1.sketch_text.stroke-203"),sQuery(id+"F0.wireOp",EDGE,"E1.sketch_text.stroke-204"),sQuery(id+"F0.wireOp",EDGE,"E1.sketch_text.stroke-205"),sQuery(id+"F0.wireOp",EDGE,"E1.sketch_text.stroke-206"),sQuery(id+"F0.wireOp",EDGE,"E1.sketch_text.stroke-207"),sQuery(id+"F0.wireOp",EDGE,"E1.sketch_text.stroke-208"),sQuery(id+"F0.wireOp",EDGE,"E1.sketch_text.stroke-209"),sQuery(id+"F0.wireOp",EDGE,"E1.sketch_text.stroke-210")])],"isStart":false}),makeQuery(id+"F4.opExtrude","SWEPT_FACE",FACE,{"disambiguationData":[OSD([sQuery(id+"F3.wireOp",EDGE,"E2.top")])]})]});
            var Q14;
            Q14=makeQuery(id+"F4.boolean.opBoolean","INTERSECT",EDGE,{"derivedFrom":[makeQuery(id+"F2.opExtrude","CAP_FACE",FACE,{"disambiguationData":[OSD([sQuery(id+"F0.wireOp",EDGE,"E0.bottom"),sQuery(id+"F0.wireOp",EDGE,"E0.top"),sQuery(id+"F0.wireOp",EDGE,"E0.left"),sQuery(id+"F0.wireOp",EDGE,"E0.right"),sQuery(id+"F0.wireOp",EDGE,"E1.sketch_text.stroke-0"),sQuery(id+"F0.wireOp",EDGE,"E1.sketch_text.stroke-1"),sQuery(id+"F0.wireOp",EDGE,"E1.sketch_text.stroke-2"),sQuery(id+"F0.wireOp",EDGE,"E1.sketch_text.stroke-3"),sQuery(id+"F0.wireOp",EDGE,"E1.sketch_text.stroke-4"),sQuery(id+"F0.wireOp",EDGE,"E1.sketch_text.stroke-5"),sQuery(id+"F0.wireOp",EDGE,"E1.sketch_text.stroke-6"),sQuery(id+"F0.wireOp",EDGE,"E1.sketch_text.stroke-7"),sQuery(id+"F0.wireOp",EDGE,"E1.sketch_text.stroke-8"),sQuery(id+"F0.wireOp",EDGE,"E1.sketch_text.stroke-9"),sQuery(id+"F0.wireOp",EDGE,"E1.sketch_text.stroke-10"),sQuery(id+"F0.wireOp",EDGE,"E1.sketch_text.stroke-11"),sQuery(id+"F0.wireOp",EDGE,"E1.sketch_text.stroke-12"),sQuery(id+"F0.wireOp",EDGE,"E1.sketch_text.stroke-13"),sQuery(id+"F0.wireOp",EDGE,"E1.sketch_text.stroke-14"),sQuery(id+"F0.wireOp",EDGE,"E1.sketch_text.stroke-15"),sQuery(id+"F0.wireOp",EDGE,"E1.sketch_text.stroke-16"),sQuery(id+"F0.wireOp",EDGE,"E1.sketch_text.stroke-17"),sQuery(id+"F0.wireOp",EDGE,"E1.sketch_text.stroke-18"),sQuery(id+"F0.wireOp",EDGE,"E1.sketch_text.stroke-19"),sQuery(id+"F0.wireOp",EDGE,"E1.sketch_text.stroke-20"),sQuery(id+"F0.wireOp",EDGE,"E1.sketch_text.stroke-21"),sQuery(id+"F0.wireOp",EDGE,"E1.sketch_text.stroke-22"),sQuery(id+"F0.wireOp",EDGE,"E1.sketch_text.stroke-23"),sQuery(id+"F0.wireOp",EDGE,"E1.sketch_text.stroke-24"),sQuery(id+"F0.wireOp",EDGE,"E1.sketch_text.stroke-25"),sQuery(id+"F0.wireOp",EDGE,"E1.sketch_text.stroke-26"),sQuery(id+"F0.wireOp",EDGE,"E1.sketch_text.stroke-27"),sQuery(id+"F0.wireOp",EDGE,"E1.sketch_text.stroke-28"),sQuery(id+"F0.wireOp",EDGE,"E1.sketch_text.stroke-29"),sQuery(id+"F0.wireOp",EDGE,"E1.sketch_text.stroke-30"),sQuery(id+"F0.wireOp",EDGE,"E1.sketch_text.stroke-31"),sQuery(id+"F0.wireOp",EDGE,"E1.sketch_text.stroke-32"),sQuery(id+"F0.wireOp",EDGE,"E1.sketch_text.stroke-33"),sQuery(id+"F0.wireOp",EDGE,"E1.sketch_text.stroke-34"),sQuery(id+"F0.wireOp",EDGE,"E1.sketch_text.stroke-35"),sQuery(id+"F0.wireOp",EDGE,"E1.sketch_text.stroke-36"),sQuery(id+"F0.wireOp",EDGE,"E1.sketch_text.stroke-37"),sQuery(id+"F0.wireOp",EDGE,"E1.sketch_text.stroke-38"),sQuery(id+"F0.wireOp",EDGE,"E1.sketch_text.stroke-39"),sQuery(id+"F0.wireOp",EDGE,"E1.sketch_text.stroke-40"),sQuery(id+"F0.wireOp",EDGE,"E1.sketch_text.stroke-41"),sQuery(id+"F0.wireOp",EDGE,"E1.sketch_text.stroke-42"),sQuery(id+"F0.wireOp",EDGE,"E1.sketch_text.stroke-43"),sQuery(id+"F0.wireOp",EDGE,"E1.sketch_text.stroke-44"),sQuery(id+"F0.wireOp",EDGE,"E1.sketch_text.stroke-45"),sQuery(id+"F0.wireOp",EDGE,"E1.sketch_text.stroke-46"),sQuery(id+"F0.wireOp",EDGE,"E1.sketch_text.stroke-47"),sQuery(id+"F0.wireOp",EDGE,"E1.sketch_text.stroke-48"),sQuery(id+"F0.wireOp",EDGE,"E1.sketch_text.stroke-49"),sQuery(id+"F0.wireOp",EDGE,"E1.sketch_text.stroke-50"),sQuery(id+"F0.wireOp",EDGE,"E1.sketch_text.stroke-51"),sQuery(id+"F0.wireOp",EDGE,"E1.sketch_text.stroke-52"),sQuery(id+"F0.wireOp",EDGE,"E1.sketch_text.stroke-53"),sQuery(id+"F0.wireOp",EDGE,"E1.sketch_text.stroke-54"),sQuery(id+"F0.wireOp",EDGE,"E1.sketch_text.stroke-55"),sQuery(id+"F0.wireOp",EDGE,"E1.sketch_text.stroke-56"),sQuery(id+"F0.wireOp",EDGE,"E1.sketch_text.stroke-57"),sQuery(id+"F0.wireOp",EDGE,"E1.sketch_text.stroke-58"),sQuery(id+"F0.wireOp",EDGE,"E1.sketch_text.stroke-59"),sQuery(id+"F0.wireOp",EDGE,"E1.sketch_text.stroke-60"),sQuery(id+"F0.wireOp",EDGE,"E1.sketch_text.stroke-61"),sQuery(id+"F0.wireOp",EDGE,"E1.sketch_text.stroke-62"),sQuery(id+"F0.wireOp",EDGE,"E1.sketch_text.stroke-63"),sQuery(id+"F0.wireOp",EDGE,"E1.sketch_text.stroke-64"),sQuery(id+"F0.wireOp",EDGE,"E1.sketch_text.stroke-65"),sQuery(id+"F0.wireOp",EDGE,"E1.sketch_text.stroke-66"),sQuery(id+"F0.wireOp",EDGE,"E1.sketch_text.stroke-67"),sQuery(id+"F0.wireOp",EDGE,"E1.sketch_text.stroke-68"),sQuery(id+"F0.wireOp",EDGE,"E1.sketch_text.stroke-69"),sQuery(id+"F0.wireOp",EDGE,"E1.sketch_text.stroke-70"),sQuery(id+"F0.wireOp",EDGE,"E1.sketch_text.stroke-71"),sQuery(id+"F0.wireOp",EDGE,"E1.sketch_text.stroke-72"),sQuery(id+"F0.wireOp",EDGE,"E1.sketch_text.stroke-73"),sQuery(id+"F0.wireOp",EDGE,"E1.sketch_text.stroke-74"),sQuery(id+"F0.wireOp",EDGE,"E1.sketch_text.stroke-75"),sQuery(id+"F0.wireOp",EDGE,"E1.sketch_text.stroke-76"),sQuery(id+"F0.wireOp",EDGE,"E1.sketch_text.stroke-77"),sQuery(id+"F0.wireOp",EDGE,"E1.sketch_text.stroke-78"),sQuery(id+"F0.wireOp",EDGE,"E1.sketch_text.stroke-79"),sQuery(id+"F0.wireOp",EDGE,"E1.sketch_text.stroke-80"),sQuery(id+"F0.wireOp",EDGE,"E1.sketch_text.stroke-81"),sQuery(id+"F0.wireOp",EDGE,"E1.sketch_text.stroke-82"),sQuery(id+"F0.wireOp",EDGE,"E1.sketch_text.stroke-83"),sQuery(id+"F0.wireOp",EDGE,"E1.sketch_text.stroke-84"),sQuery(id+"F0.wireOp",EDGE,"E1.sketch_text.stroke-85"),sQuery(id+"F0.wireOp",EDGE,"E1.sketch_text.stroke-86"),sQuery(id+"F0.wireOp",EDGE,"E1.sketch_text.stroke-87"),sQuery(id+"F0.wireOp",EDGE,"E1.sketch_text.stroke-88"),sQuery(id+"F0.wireOp",EDGE,"E1.sketch_text.stroke-89"),sQuery(id+"F0.wireOp",EDGE,"E1.sketch_text.stroke-90"),sQuery(id+"F0.wireOp",EDGE,"E1.sketch_text.stroke-91"),sQuery(id+"F0.wireOp",EDGE,"E1.sketch_text.stroke-92"),sQuery(id+"F0.wireOp",EDGE,"E1.sketch_text.stroke-93"),sQuery(id+"F0.wireOp",EDGE,"E1.sketch_text.stroke-94"),sQuery(id+"F0.wireOp",EDGE,"E1.sketch_text.stroke-95"),sQuery(id+"F0.wireOp",EDGE,"E1.sketch_text.stroke-96"),sQuery(id+"F0.wireOp",EDGE,"E1.sketch_text.stroke-97"),sQuery(id+"F0.wireOp",EDGE,"E1.sketch_text.stroke-98"),sQuery(id+"F0.wireOp",EDGE,"E1.sketch_text.stroke-99"),sQuery(id+"F0.wireOp",EDGE,"E1.sketch_text.stroke-100"),sQuery(id+"F0.wireOp",EDGE,"E1.sketch_text.stroke-101"),sQuery(id+"F0.wireOp",EDGE,"E1.sketch_text.stroke-102"),sQuery(id+"F0.wireOp",EDGE,"E1.sketch_text.stroke-103"),sQuery(id+"F0.wireOp",EDGE,"E1.sketch_text.stroke-112"),sQuery(id+"F0.wireOp",EDGE,"E1.sketch_text.stroke-113"),sQuery(id+"F0.wireOp",EDGE,"E1.sketch_text.stroke-114"),sQuery(id+"F0.wireOp",EDGE,"E1.sketch_text.stroke-115"),sQuery(id+"F0.wireOp",EDGE,"E1.sketch_text.stroke-116"),sQuery(id+"F0.wireOp",EDGE,"E1.sketch_text.stroke-117"),sQuery(id+"F0.wireOp",EDGE,"E1.sketch_text.stroke-118"),sQuery(id+"F0.wireOp",EDGE,"E1.sketch_text.stroke-119"),sQuery(id+"F0.wireOp",EDGE,"E1.sketch_text.stroke-120"),sQuery(id+"F0.wireOp",EDGE,"E1.sketch_text.stroke-121"),sQuery(id+"F0.wireOp",EDGE,"E1.sketch_text.stroke-122"),sQuery(id+"F0.wireOp",EDGE,"E1.sketch_text.stroke-123"),sQuery(id+"F0.wireOp",EDGE,"E1.sketch_text.stroke-124"),sQuery(id+"F0.wireOp",EDGE,"E1.sketch_text.stroke-125"),sQuery(id+"F0.wireOp",EDGE,"E1.sketch_text.stroke-126"),sQuery(id+"F0.wireOp",EDGE,"E1.sketch_text.stroke-127"),sQuery(id+"F0.wireOp",EDGE,"E1.sketch_text.stroke-128"),sQuery(id+"F0.wireOp",EDGE,"E1.sketch_text.stroke-129"),sQuery(id+"F0.wireOp",EDGE,"E1.sketch_text.stroke-130"),sQuery(id+"F0.wireOp",EDGE,"E1.sketch_text.stroke-131"),sQuery(id+"F0.wireOp",EDGE,"E1.sketch_text.stroke-132"),sQuery(id+"F0.wireOp",EDGE,"E1.sketch_text.stroke-133"),sQuery(id+"F0.wireOp",EDGE,"E1.sketch_text.stroke-134"),sQuery(id+"F0.wireOp",EDGE,"E1.sketch_text.stroke-135"),sQuery(id+"F0.wireOp",EDGE,"E1.sketch_text.stroke-136"),sQuery(id+"F0.wireOp",EDGE,"E1.sketch_text.stroke-137"),sQuery(id+"F0.wireOp",EDGE,"E1.sketch_text.stroke-138"),sQuery(id+"F0.wireOp",EDGE,"E1.sketch_text.stroke-139"),sQuery(id+"F0.wireOp",EDGE,"E1.sketch_text.stroke-140"),sQuery(id+"F0.wireOp",EDGE,"E1.sketch_text.stroke-141"),sQuery(id+"F0.wireOp",EDGE,"E1.sketch_text.stroke-142"),sQuery(id+"F0.wireOp",EDGE,"E1.sketch_text.stroke-143"),sQuery(id+"F0.wireOp",EDGE,"E1.sketch_text.stroke-144"),sQuery(id+"F0.wireOp",EDGE,"E1.sketch_text.stroke-145"),sQuery(id+"F0.wireOp",EDGE,"E1.sketch_text.stroke-146"),sQuery(id+"F0.wireOp",EDGE,"E1.sketch_text.stroke-147"),sQuery(id+"F0.wireOp",EDGE,"E1.sketch_text.stroke-148"),sQuery(id+"F0.wireOp",EDGE,"E1.sketch_text.stroke-149"),sQuery(id+"F0.wireOp",EDGE,"E1.sketch_text.stroke-150"),sQuery(id+"F0.wireOp",EDGE,"E1.sketch_text.stroke-151"),sQuery(id+"F0.wireOp",EDGE,"E1.sketch_text.stroke-152"),sQuery(id+"F0.wireOp",EDGE,"E1.sketch_text.stroke-153"),sQuery(id+"F0.wireOp",EDGE,"E1.sketch_text.stroke-154"),sQuery(id+"F0.wireOp",EDGE,"E1.sketch_text.stroke-155"),sQuery(id+"F0.wireOp",EDGE,"E1.sketch_text.stroke-156"),sQuery(id+"F0.wireOp",EDGE,"E1.sketch_text.stroke-157"),sQuery(id+"F0.wireOp",EDGE,"E1.sketch_text.stroke-158"),sQuery(id+"F0.wireOp",EDGE,"E1.sketch_text.stroke-159"),sQuery(id+"F0.wireOp",EDGE,"E1.sketch_text.stroke-160"),sQuery(id+"F0.wireOp",EDGE,"E1.sketch_text.stroke-161"),sQuery(id+"F0.wireOp",EDGE,"E1.sketch_text.stroke-162"),sQuery(id+"F0.wireOp",EDGE,"E1.sketch_text.stroke-163"),sQuery(id+"F0.wireOp",EDGE,"E1.sketch_text.stroke-164"),sQuery(id+"F0.wireOp",EDGE,"E1.sketch_text.stroke-165"),sQuery(id+"F0.wireOp",EDGE,"E1.sketch_text.stroke-166"),sQuery(id+"F0.wireOp",EDGE,"E1.sketch_text.stroke-167"),sQuery(id+"F0.wireOp",EDGE,"E1.sketch_text.stroke-168"),sQuery(id+"F0.wireOp",EDGE,"E1.sketch_text.stroke-169"),sQuery(id+"F0.wireOp",EDGE,"E1.sketch_text.stroke-170"),sQuery(id+"F0.wireOp",EDGE,"E1.sketch_text.stroke-171"),sQuery(id+"F0.wireOp",EDGE,"E1.sketch_text.stroke-172"),sQuery(id+"F0.wireOp",EDGE,"E1.sketch_text.stroke-173"),sQuery(id+"F0.wireOp",EDGE,"E1.sketch_text.stroke-174"),sQuery(id+"F0.wireOp",EDGE,"E1.sketch_text.stroke-175"),sQuery(id+"F0.wireOp",EDGE,"E1.sketch_text.stroke-176"),sQuery(id+"F0.wireOp",EDGE,"E1.sketch_text.stroke-185"),sQuery(id+"F0.wireOp",EDGE,"E1.sketch_text.stroke-186"),sQuery(id+"F0.wireOp",EDGE,"E1.sketch_text.stroke-187"),sQuery(id+"F0.wireOp",EDGE,"E1.sketch_text.stroke-188"),sQuery(id+"F0.wireOp",EDGE,"E1.sketch_text.stroke-189"),sQuery(id+"F0.wireOp",EDGE,"E1.sketch_text.stroke-190"),sQuery(id+"F0.wireOp",EDGE,"E1.sketch_text.stroke-191"),sQuery(id+"F0.wireOp",EDGE,"E1.sketch_text.stroke-192"),sQuery(id+"F0.wireOp",EDGE,"E1.sketch_text.stroke-193"),sQuery(id+"F0.wireOp",EDGE,"E1.sketch_text.stroke-194"),sQuery(id+"F0.wireOp",EDGE,"E1.sketch_text.stroke-195"),sQuery(id+"F0.wireOp",EDGE,"E1.sketch_text.stroke-196"),sQuery(id+"F0.wireOp",EDGE,"E1.sketch_text.stroke-197"),sQuery(id+"F0.wireOp",EDGE,"E1.sketch_text.stroke-198"),sQuery(id+"F0.wireOp",EDGE,"E1.sketch_text.stroke-199"),sQuery(id+"F0.wireOp",EDGE,"E1.sketch_text.stroke-200"),sQuery(id+"F0.wireOp",EDGE,"E1.sketch_text.stroke-201"),sQuery(id+"F0.wireOp",EDGE,"E1.sketch_text.stroke-202"),sQuery(id+"F0.wireOp",EDGE,"E1.sketch_text.stroke-203"),sQuery(id+"F0.wireOp",EDGE,"E1.sketch_text.stroke-204"),sQuery(id+"F0.wireOp",EDGE,"E1.sketch_text.stroke-205"),sQuery(id+"F0.wireOp",EDGE,"E1.sketch_text.stroke-206"),sQuery(id+"F0.wireOp",EDGE,"E1.sketch_text.stroke-207"),sQuery(id+"F0.wireOp",EDGE,"E1.sketch_text.stroke-208"),sQuery(id+"F0.wireOp",EDGE,"E1.sketch_text.stroke-209"),sQuery(id+"F0.wireOp",EDGE,"E1.sketch_text.stroke-210")])],"isStart":false}),makeQuery(id+"F4.opExtrude","SWEPT_FACE",FACE,{"disambiguationData":[OSD([sQuery(id+"F3.wireOp",EDGE,"E2.right")])]})]});
            fillet(context, id + "F5", {"entities" : qUnion([Q0, Q1, Q2, Q3, Q4, Q5, Q6, Q7, Q8, Q9, Q10, Q11, Q12, Q13, Q14]), "radius" : 5 * mm, "tangentPropagation" : true, "allowEdgeOverflow" : false});
        }
    });
